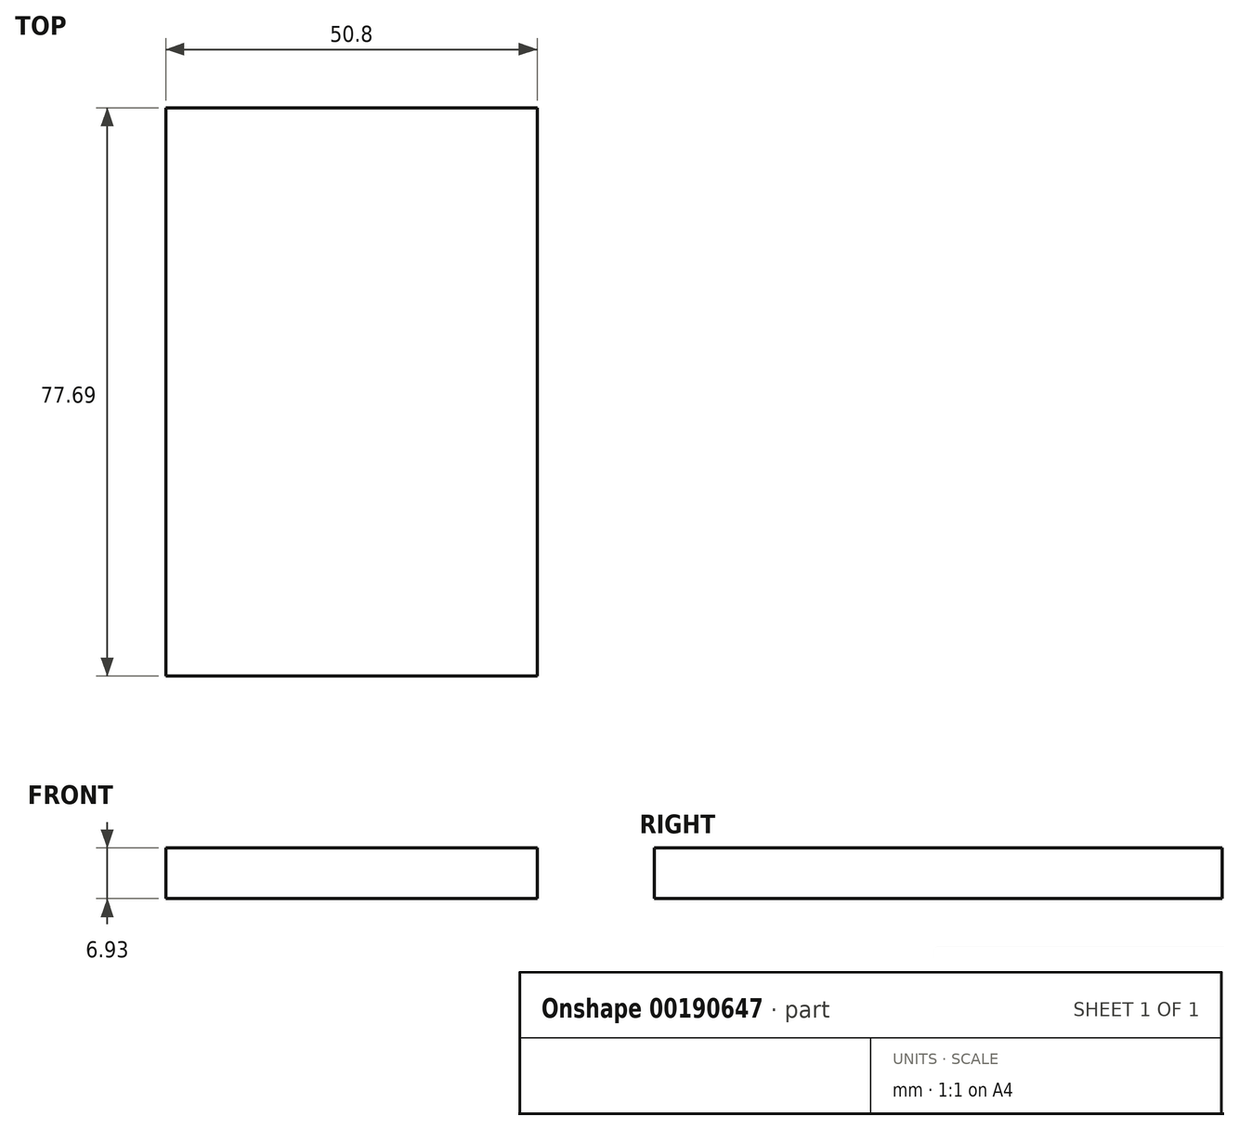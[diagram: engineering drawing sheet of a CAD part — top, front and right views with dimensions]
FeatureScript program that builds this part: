
annotation { "Feature Type Name" : "Feature", "Feature Type Description" : "" }
export const myFeature = defineFeature(function(context is Context, id is Id, definition is map)
    precondition{}
    {
        {
            var Q0;
            Q0=qCreatedBy(makeId("Right.planeOp"),FACE);
            var sketch = newSketch(context, id + "F0", { "sketchPlane" : qUnion([Q0])});
            skLineSegment(sketch, "E0.bottom", {"start": v(-31.34, 7.25) * mm, "end": v(46.35, 7.25) * mm});
            skLineSegment(sketch, "E0.top", {"start": v(-31.34, 0.32) * mm, "end": v(46.35, 0.32) * mm});
            skLineSegment(sketch, "E0.left", {"start": v(-31.34, 7.25) * mm, "end": v(-31.34, 0.32) * mm});
            skLineSegment(sketch, "E0.right", {"start": v(46.35, 7.25) * mm, "end": v(46.35, 0.32) * mm});
            skSolve(sketch);
        }
        {
            var Q0;
            Q0 = qSketchRegion(id + "F0", true);
            extrude(context, id + "F1", {"entities" : qUnion([Q0]), "depth" : 50.8 * mm});
        }
    });
